# Revit family: DOP48M96D_Revit
name_source: partatom
category: Specialty Equipment
revit_build: Autodesk Revit MEP 2014 (Build: 20130308_1515(x64)
units: mm (PartAtom-declared; Revit-internal decimal feet)

## types (1)
- DOP48M96D
    AMBIENT LIGHTING = YES (DIMMING)
    Adjustment = Stainless Steel
    BAKE ELEMENT = 3,000W - 8 PASS (LG) 1,000W (SM)
    BLACK BURNER CAPS = YES
    BLUETOOTH (HOOD CONNECTION) = YES
    BRASS BURNER CAPS = YES
    BROIL ELEMENT = 4,400W - 10 PASS (LG) 2,400W (SM)
    Burner = Plastic-Black
    CENTER FRONT (BTU) = 22,000 DUAL (SIMMER)
    CENTER REAR (BTU) = 9,000 STACK DUAL (SIMMER)
    CHILD LOCK = YES
    CLOCK = YES
    CONTROL METHOD = 7” POP-UP LCD
    CONVECTION ELEMENT = 1,300W (EA - 2,600W TOTAL) (LG) / 2,000W (SM)
    CONVECTION FILTER = 2 (LG) / 1 (SM)
    COOKIE SHEETS (SET OF 3) = SKU - ACSM303
    COOKING MODES LARGE CAVITY = BAKE - BROIL - CONVECTION BAKE - CONVECTION ROAST - CONVECTION BROIL - FOUR-PART PURE CONVECTION - PURE CONVECTION SEAR
    COOKING MODES SMALL CAVITY = BAKE - BROIL - CONVECTION BAKE - CONVECTION ROAST - CONVECTION BROIL - FOUR-PART PURE CONVECTION - REAL STEAM - STEAM BAKE - STEAM ROAST
    DELAY START = YES
    Depth = 24"
    Description = 48-INCH PRO DUAL-FUEL STEAM RANGE MODERNIST COLLECTION
    Door = Plastic-Black
    GLIDERACK™ = 2 (LG)
    Gas Burner = Stainless Steel
    Glide = Plastic-Black
    HALF STEAM TRAY = 2 (SM)
    HIGHLIGHTING COLOR = WHITE
    Handle = Stainless Steel
    Height = 36 1/2"
    ILLULMINA™ BURNER KNOBS = YES
    INFOCENTER™ DISPLAY = YES
    KITCHEN TIMER = YES
    LEFT FRONT (BTU) = 18,000 DUAL (SIMMER)
    LEFT REAR (BTU) = 16,000 STACK DUAL (SIMMER)
    MANUAL LIGHTING ON/OFF = YES
    Manufacturer = Dacor
    Model = DOP48M96D
    NUMBER OF KNOBS = 7 + 2 LAMP KNOBS
    OVEN CAPACITY (CUBIC FEET) = 4.8 (LG OVEN) / 1.8 (SM OVEN)
    PERMA-FLAME™ (AUTO RE-IGNITION) = YES
    POWER OF GRIDDLE = 1,400W
    RIGHT FRONT (BTU) = 16,000 STACK DUAL (SIMMER)
    RIGHT REAR (BTU) = 16,000 STACK DUAL (SIMMER)
    SEALED BURNERS = YES
    SOUND ON/OFF = YES
    STANDARD RACK = 1 (LG) / 1 (SM)
    STEAM HEATER = 2,000W (SM)
    STEAM TRAY = 2 (SM)
    Support = Glass
    TEMPERATURE (F / C) = YES
    TEMPERATURE PROBE = 1 EA (BOTH)
    TIME OF DAY (12 HR/24 HR) = YES
    TOTAL NUMBER OF COOKTOP BURNERS = 6 + GRIDDLE
    Unit = Stainless Steel
    WI FI = YES
    WOK RING = 1
    Width = 48"

## geometry (parser evidence)
native form markers: Blend x4, Sweep x2
no freeform markers — native parametric forms only
